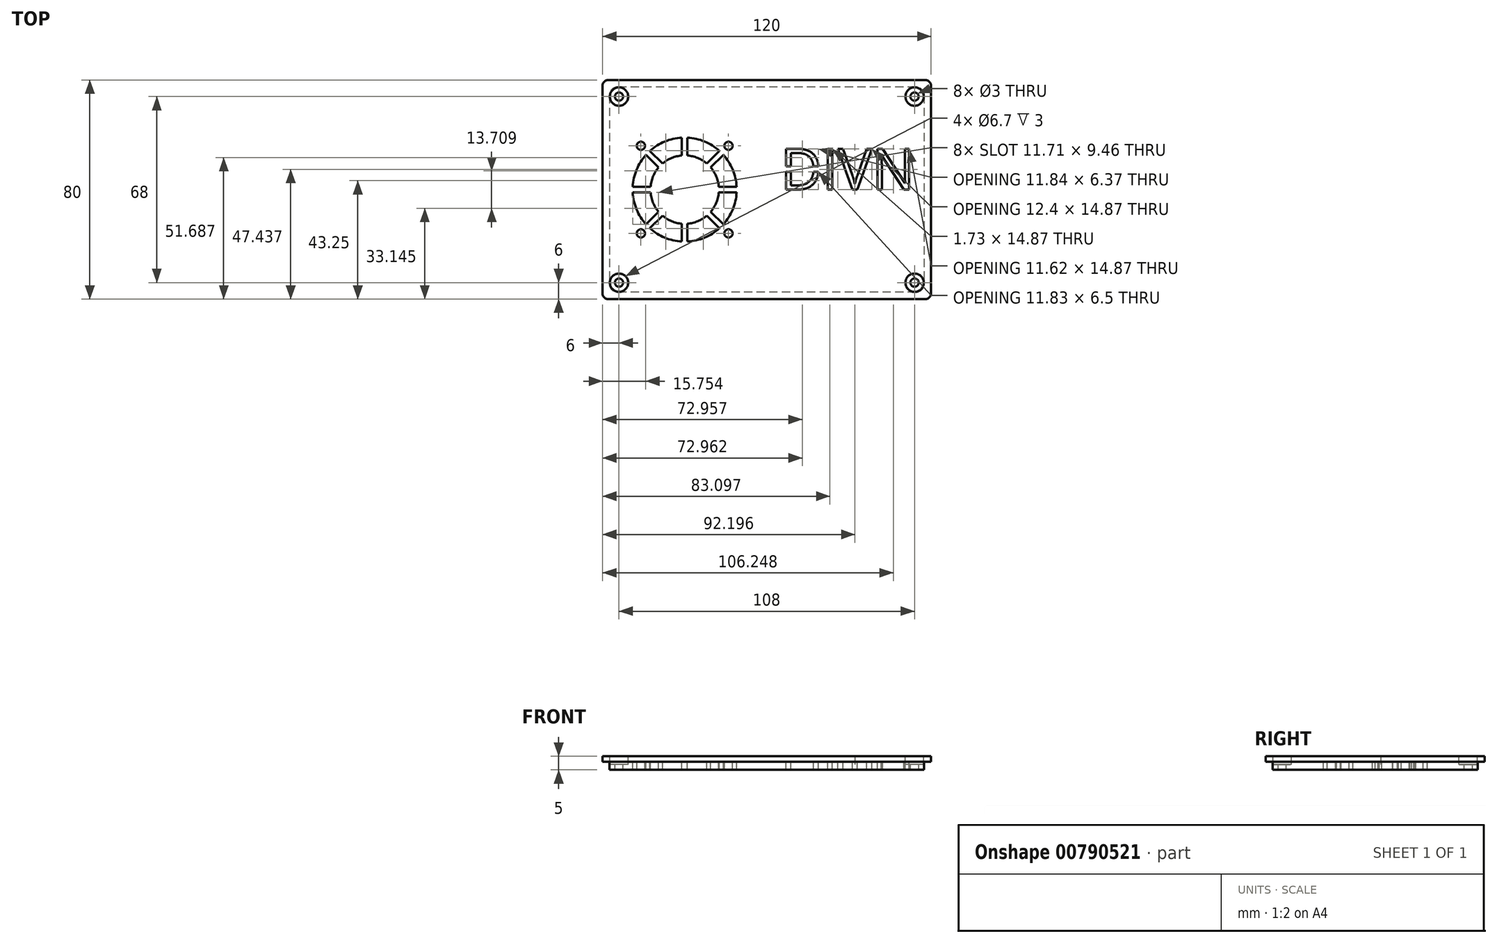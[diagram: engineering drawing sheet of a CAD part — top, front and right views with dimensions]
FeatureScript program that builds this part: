
annotation { "Feature Type Name" : "Feature", "Feature Type Description" : "" }
export const myFeature = defineFeature(function(context is Context, id is Id, definition is map)
    precondition{}
    {
        {
            var Q0;
            Q0=qCreatedBy(makeId("Top.planeOp"),FACE);
            var sketch = newSketch(context, id + "F0", { "sketchPlane" : qUnion([Q0])});
            skLineSegment(sketch, "E0.bottom", {"start": v(60, 40) * mm, "end": v(-60, 40) * mm});
            skLineSegment(sketch, "E0.top", {"start": v(60, -40) * mm, "end": v(-60, -40) * mm});
            skLineSegment(sketch, "E0.left", {"start": v(60, 40) * mm, "end": v(60, -40) * mm});
            skLineSegment(sketch, "E0.right", {"start": v(-60, 40) * mm, "end": v(-60, -40) * mm});
            skPoint(sketch, "E0.middle", {"position": v(0, 0) * mm});
            skLineSegment(sketch, "E1.bottom", {"start": v(57.5, 37.5) * mm, "end": v(-57.5, 37.5) * mm});
            skLineSegment(sketch, "E1.top", {"start": v(57.5, -37.5) * mm, "end": v(-57.5, -37.5) * mm});
            skLineSegment(sketch, "E1.left", {"start": v(57.5, 37.5) * mm, "end": v(57.5, -37.5) * mm});
            skLineSegment(sketch, "E1.right", {"start": v(-57.5, 37.5) * mm, "end": v(-57.5, -37.5) * mm});
            skSolve(sketch);
        }
        {
            var Q0;
            Q0=makeQuery(id+"F0.imprint","IMPRINT",FACE,{"disambiguationData":[TD([[makeQuery(id+"F0.imprint","IMPRINT",EDGE,{"derivedFrom":sQuery(id+"F0.wireOp",EDGE,"E0.bottom")}),1.0]])]});
            extrude(context, id + "F1", {"entities" : qUnion([Q0]), "depth" : 2 * mm, "offsetDistance" : 25 * mm});
        }
        {
            var Q0;
            Q0=makeQuery(id+"F1.opExtrude","CAP_FACE",FACE,{"disambiguationData":[OSD([sQuery(id+"F0.wireOp",EDGE,"E0.bottom"),sQuery(id+"F0.wireOp",EDGE,"E0.top"),sQuery(id+"F0.wireOp",EDGE,"E0.left"),sQuery(id+"F0.wireOp",EDGE,"E0.right"),sQuery(id+"F0.wireOp",EDGE,"E1.bottom"),sQuery(id+"F0.wireOp",EDGE,"E1.top"),sQuery(id+"F0.wireOp",EDGE,"E1.left"),sQuery(id+"F0.wireOp",EDGE,"E1.right")])],"isStart":false});
            var sketch = newSketch(context, id + "F2", { "sketchPlane" : qUnion([Q0])});
            skLineSegment(sketch, "E2.bottom", {"start": v(-57.5, 37.5) * mm, "end": v(57.5, 37.5) * mm});
            skLineSegment(sketch, "E2.top", {"start": v(-57.5, -37.5) * mm, "end": v(57.5, -37.5) * mm});
            skLineSegment(sketch, "E2.left", {"start": v(-57.5, 37.5) * mm, "end": v(-57.5, -37.5) * mm});
            skLineSegment(sketch, "E2.right", {"start": v(57.5, 37.5) * mm, "end": v(57.5, -37.5) * mm});
            skSolve(sketch);
        }
        {
            var Q0;
            Q0=makeQuery(id+"F2.imprint","IMPRINT",FACE,{"disambiguationData":[TD([[makeQuery(id+"F2.imprint","IMPRINT",EDGE,{"derivedFrom":sQuery(id+"F2.wireOp",EDGE,"E2.bottom")}),1.0]])]});
            extrude(context, id + "F3", {"entities" : qUnion([Q0]), "oppositeDirection" : true, "depth" : 5 * mm, "offsetDistance" : 25 * mm});
        }
        {
            var Q0;
            Q0=makeQuery(id+"F3.opExtrude","SWEPT_BODY",BODY,{"disambiguationData":[OSD([sQuery(id+"F2.wireOp",EDGE,"E2.bottom"),sQuery(id+"F2.wireOp",EDGE,"E2.top"),sQuery(id+"F2.wireOp",EDGE,"E2.left"),sQuery(id+"F2.wireOp",EDGE,"E2.right")])]});
            var Q1;
            Q1=makeQuery(id+"F1.opExtrude","SWEPT_BODY",BODY,{"disambiguationData":[OSD([sQuery(id+"F0.wireOp",EDGE,"E0.bottom"),sQuery(id+"F0.wireOp",EDGE,"E0.top"),sQuery(id+"F0.wireOp",EDGE,"E0.left"),sQuery(id+"F0.wireOp",EDGE,"E0.right"),sQuery(id+"F0.wireOp",EDGE,"E1.bottom"),sQuery(id+"F0.wireOp",EDGE,"E1.top"),sQuery(id+"F0.wireOp",EDGE,"E1.left"),sQuery(id+"F0.wireOp",EDGE,"E1.right")])]});
            booleanBodies(context, id + "F4", {"operationType" : BooleanOperationType.UNION, "tools" : qUnion([Q0, Q1])});
        }
        {
            var Q0;
            Q0=makeQuery(id+"F3.opExtrude","SWEPT_EDGE",EDGE,{"disambiguationData":[OSD([sQuery(id+"F2.wireOp",EDGE,"E2.bottom"),sQuery(id+"F2.wireOp",EDGE,"E2.left")])]});
            var Q1;
            Q1=makeQuery(id+"F3.opExtrude","SWEPT_EDGE",EDGE,{"disambiguationData":[OSD([sQuery(id+"F2.wireOp",EDGE,"E2.top"),sQuery(id+"F2.wireOp",EDGE,"E2.left")])]});
            var Q2;
            Q2=makeQuery(id+"F3.opExtrude","SWEPT_EDGE",EDGE,{"disambiguationData":[OSD([sQuery(id+"F2.wireOp",EDGE,"E2.top"),sQuery(id+"F2.wireOp",EDGE,"E2.right")])]});
            var Q3;
            Q3=makeQuery(id+"F3.opExtrude","SWEPT_EDGE",EDGE,{"disambiguationData":[OSD([sQuery(id+"F2.wireOp",EDGE,"E2.bottom"),sQuery(id+"F2.wireOp",EDGE,"E2.right")])]});
            fillet(context, id + "F5", {"entities" : qUnion([Q0, Q1, Q2, Q3]), "radius" : 3 * mm, "tangentPropagation" : true, "allowEdgeOverflow" : false});
        }
        {
            var Q0;
            Q0=makeQuery(id+"F1.opExtrude","SWEPT_EDGE",EDGE,{"disambiguationData":[OSD([sQuery(id+"F0.wireOp",EDGE,"E0.bottom"),sQuery(id+"F0.wireOp",EDGE,"E0.left")])]});
            var Q1;
            Q1=makeQuery(id+"F1.opExtrude","SWEPT_EDGE",EDGE,{"disambiguationData":[OSD([sQuery(id+"F0.wireOp",EDGE,"E0.top"),sQuery(id+"F0.wireOp",EDGE,"E0.left")])]});
            var Q2;
            Q2=makeQuery(id+"F1.opExtrude","SWEPT_EDGE",EDGE,{"disambiguationData":[OSD([sQuery(id+"F0.wireOp",EDGE,"E0.top"),sQuery(id+"F0.wireOp",EDGE,"E0.right")])]});
            var Q3;
            Q3=makeQuery(id+"F1.opExtrude","SWEPT_EDGE",EDGE,{"disambiguationData":[OSD([sQuery(id+"F0.wireOp",EDGE,"E0.bottom"),sQuery(id+"F0.wireOp",EDGE,"E0.right")])]});
            fillet(context, id + "F6", {"entities" : qUnion([Q0, Q1, Q2, Q3]), "radius" : 2 * mm, "tangentPropagation" : true, "allowEdgeOverflow" : false});
        }
        {
            var Q0;
            Q0=makeQuery(id+"F4.opBoolean","MERGE",FACE,{"derivedFrom":[makeQuery(id+"F1.opExtrude","CAP_FACE",FACE,{"disambiguationData":[OSD([sQuery(id+"F0.wireOp",EDGE,"E0.bottom"),sQuery(id+"F0.wireOp",EDGE,"E0.top"),sQuery(id+"F0.wireOp",EDGE,"E0.left"),sQuery(id+"F0.wireOp",EDGE,"E0.right"),sQuery(id+"F0.wireOp",EDGE,"E1.bottom"),sQuery(id+"F0.wireOp",EDGE,"E1.top"),sQuery(id+"F0.wireOp",EDGE,"E1.left"),sQuery(id+"F0.wireOp",EDGE,"E1.right")])],"isStart":false}),makeQuery(id+"F3.opExtrude","CAP_FACE",FACE,{"disambiguationData":[OSD([sQuery(id+"F2.wireOp",EDGE,"E2.bottom"),sQuery(id+"F2.wireOp",EDGE,"E2.top"),sQuery(id+"F2.wireOp",EDGE,"E2.left"),sQuery(id+"F2.wireOp",EDGE,"E2.right")])],"isStart":true})]});
            var sketch = newSketch(context, id + "F7", { "sketchPlane" : qUnion([Q0])});
            skCircle(sketch, "E3", {"center": v(-54, 34) * mm, "radius": 1.5 * mm});
            skCircle(sketch, "E4", {"center": v(54, 34) * mm, "radius": 1.5 * mm});
            skCircle(sketch, "E5", {"center": v(54, -34) * mm, "radius": 1.5 * mm});
            skCircle(sketch, "E6", {"center": v(-54, -34) * mm, "radius": 1.5 * mm});
            skPoint(sketch, "E7.middle", {"position": v(-30, 0) * mm});
            skPoint(sketch, "E8.middle", {"position": v(25.11, 0) * mm});
            skSolve(sketch);
        }
        {
            var Q0;
            Q0=makeQuery(id+"F7.imprint","IMPRINT",FACE,{"disambiguationData":[TD([[makeQuery(id+"F7.imprint","IMPRINT",EDGE,{"derivedFrom":sQuery(id+"F7.wireOp",EDGE,"E3")}),1.0]])]});
            var Q1;
            Q1=makeQuery(id+"F7.imprint","IMPRINT",FACE,{"disambiguationData":[TD([[makeQuery(id+"F7.imprint","IMPRINT",EDGE,{"derivedFrom":sQuery(id+"F7.wireOp",EDGE,"E4")}),1.0]])]});
            var Q2;
            Q2=makeQuery(id+"F7.imprint","IMPRINT",FACE,{"disambiguationData":[TD([[makeQuery(id+"F7.imprint","IMPRINT",EDGE,{"derivedFrom":sQuery(id+"F7.wireOp",EDGE,"E6")}),1.0]])]});
            var Q3;
            Q3=makeQuery(id+"F7.imprint","IMPRINT",FACE,{"disambiguationData":[TD([[makeQuery(id+"F7.imprint","IMPRINT",EDGE,{"derivedFrom":sQuery(id+"F7.wireOp",EDGE,"E5")}),1.0]])]});
            var Q4;
            Q4=sQuery(id+"F7.wireOp",EDGE,"E3");
            var Q5;
            Q5=sQuery(id+"F7.wireOp",EDGE,"E4");
            var Q6;
            Q6=sQuery(id+"F7.wireOp",EDGE,"E5");
            var Q7;
            Q7=sQuery(id+"F7.wireOp",EDGE,"E6");
            extrude(context, id + "F8", {"entities" : qUnion([Q0, Q1, Q2, Q3]), "operationType" : NewBodyOperationType.REMOVE, "surfaceEntities" : qUnion([Q4, Q5, Q6, Q7]), "oppositeDirection" : true, "depth" : 25 * mm, "offsetDistance" : 25 * mm});
        }
        {
            var Q0;
            Q0=makeQuery(id+"F4.opBoolean","MERGE",FACE,{"derivedFrom":[makeQuery(id+"F1.opExtrude","CAP_FACE",FACE,{"disambiguationData":[OSD([sQuery(id+"F0.wireOp",EDGE,"E0.bottom"),sQuery(id+"F0.wireOp",EDGE,"E0.top"),sQuery(id+"F0.wireOp",EDGE,"E0.left"),sQuery(id+"F0.wireOp",EDGE,"E0.right"),sQuery(id+"F0.wireOp",EDGE,"E1.bottom"),sQuery(id+"F0.wireOp",EDGE,"E1.top"),sQuery(id+"F0.wireOp",EDGE,"E1.left"),sQuery(id+"F0.wireOp",EDGE,"E1.right")])],"isStart":false}),makeQuery(id+"F3.opExtrude","CAP_FACE",FACE,{"disambiguationData":[OSD([sQuery(id+"F2.wireOp",EDGE,"E2.bottom"),sQuery(id+"F2.wireOp",EDGE,"E2.top"),sQuery(id+"F2.wireOp",EDGE,"E2.left"),sQuery(id+"F2.wireOp",EDGE,"E2.right")])],"isStart":true})]});
            var sketch = newSketch(context, id + "F9", { "sketchPlane" : qUnion([Q0])});
            skCircle(sketch, "E9", {"center": v(-54, 34) * mm, "radius": 3.35 * mm});
            skCircle(sketch, "E10", {"center": v(54, 34) * mm, "radius": 3.35 * mm});
            skCircle(sketch, "E11", {"center": v(54, -34) * mm, "radius": 3.35 * mm});
            skCircle(sketch, "E12", {"center": v(-54, -34) * mm, "radius": 3.35 * mm});
            skSolve(sketch);
        }
        {
            var Q0;
            Q0=makeQuery(id+"F9.imprint","IMPRINT",FACE,{"disambiguationData":[TD([[makeQuery(id+"F9.imprint","IMPRINT",EDGE,{"derivedFrom":sQuery(id+"F9.wireOp",EDGE,"E9")}),1.0]])]});
            var Q1;
            Q1=makeQuery(id+"F9.imprint","IMPRINT",FACE,{"disambiguationData":[TD([[makeQuery(id+"F9.imprint","IMPRINT",EDGE,{"derivedFrom":sQuery(id+"F9.wireOp",EDGE,"E10")}),1.0]])]});
            var Q2;
            Q2=makeQuery(id+"F9.imprint","IMPRINT",FACE,{"disambiguationData":[TD([[makeQuery(id+"F9.imprint","IMPRINT",EDGE,{"derivedFrom":sQuery(id+"F9.wireOp",EDGE,"E11")}),1.0]])]});
            var Q3;
            Q3=makeQuery(id+"F9.imprint","IMPRINT",FACE,{"disambiguationData":[TD([[makeQuery(id+"F9.imprint","IMPRINT",EDGE,{"derivedFrom":sQuery(id+"F9.wireOp",EDGE,"E12")}),1.0]])]});
            extrude(context, id + "F10", {"entities" : qUnion([Q0, Q1, Q2, Q3]), "operationType" : NewBodyOperationType.REMOVE, "oppositeDirection" : true, "depth" : 3 * mm, "offsetDistance" : 25 * mm});
        }
        {
            var Q0;
            Q0=makeQuery(id+"F4.opBoolean","MERGE",FACE,{"derivedFrom":[makeQuery(id+"F1.opExtrude","CAP_FACE",FACE,{"disambiguationData":[OSD([sQuery(id+"F0.wireOp",EDGE,"E0.bottom"),sQuery(id+"F0.wireOp",EDGE,"E0.top"),sQuery(id+"F0.wireOp",EDGE,"E0.left"),sQuery(id+"F0.wireOp",EDGE,"E0.right"),sQuery(id+"F0.wireOp",EDGE,"E1.bottom"),sQuery(id+"F0.wireOp",EDGE,"E1.top"),sQuery(id+"F0.wireOp",EDGE,"E1.left"),sQuery(id+"F0.wireOp",EDGE,"E1.right")])],"isStart":false}),makeQuery(id+"F3.opExtrude","CAP_FACE",FACE,{"disambiguationData":[OSD([sQuery(id+"F2.wireOp",EDGE,"E2.bottom"),sQuery(id+"F2.wireOp",EDGE,"E2.top"),sQuery(id+"F2.wireOp",EDGE,"E2.left"),sQuery(id+"F2.wireOp",EDGE,"E2.right")])],"isStart":true})]});
            var sketch = newSketch(context, id + "F11", { "sketchPlane" : qUnion([Q0])});
            skLineSegment(sketch, "E13.bottom", {"start": v(-50, 20) * mm, "end": v(-10, 20) * mm, "construction": true});
            skLineSegment(sketch, "E13.top", {"start": v(-50, -20) * mm, "end": v(-10, -20) * mm, "construction": true});
            skLineSegment(sketch, "E13.left", {"start": v(-50, 20) * mm, "end": v(-50, -20) * mm, "construction": true});
            skLineSegment(sketch, "E13.right", {"start": v(-10, 20) * mm, "end": v(-10, -20) * mm, "construction": true});
            skCircle(sketch, "E14", {"center": v(-46, 16) * mm, "radius": 1.5 * mm});
            skCircle(sketch, "E15", {"center": v(-14, 16) * mm, "radius": 1.5 * mm});
            skCircle(sketch, "E16", {"center": v(-14, -16) * mm, "radius": 1.5 * mm});
            skCircle(sketch, "E17", {"center": v(-46, -16) * mm, "radius": 1.5 * mm});
            skCircle(sketch, "E18", {"center": v(-30, 0) * mm, "radius": 19 * mm});
            skPoint(sketch, "E18.centerSnap0", {"position": v(-30, 20) * mm});
            skPoint(sketch, "E18.centerSnap1", {"position": v(-10, 0) * mm});
            skCircle(sketch, "E19", {"center": v(-30, 0) * mm, "radius": 12.5 * mm});
            skLineSegment(sketch, "E20.bottom", {"start": v(-29, 19.5) * mm, "end": v(-31, 19.5) * mm});
            skLineSegment(sketch, "E20.top", {"start": v(-29, 12) * mm, "end": v(-31, 12) * mm});
            skLineSegment(sketch, "E20.left", {"start": v(-29, 19.5) * mm, "end": v(-29, 12) * mm});
            skLineSegment(sketch, "E20.right", {"start": v(-31, 19.5) * mm, "end": v(-31, 12) * mm});
            skPoint(sketch, "E20.middle", {"position": v(-30, 15.75) * mm});
            skPoint(sketch, "E21.1.0", {"position": v(-41.14, 11.14) * mm});
            skLineSegment(sketch, "E21.1.1", {"start": v(-43.08, 14.5) * mm, "end": v(-44.5, 13.08) * mm});
            skLineSegment(sketch, "E21.1.2", {"start": v(-44.5, 13.08) * mm, "end": v(-39.2, 7.78) * mm});
            skLineSegment(sketch, "E21.1.3", {"start": v(-43.08, 14.5) * mm, "end": v(-37.78, 9.2) * mm});
            skLineSegment(sketch, "E21.1.4", {"start": v(-37.78, 9.2) * mm, "end": v(-39.2, 7.78) * mm});
            skPoint(sketch, "E21.2.0", {"position": v(-45.75, 0) * mm});
            skLineSegment(sketch, "E21.2.1", {"start": v(-49.5, 1) * mm, "end": v(-49.5, -1) * mm});
            skLineSegment(sketch, "E21.2.2", {"start": v(-49.5, -1) * mm, "end": v(-42, -1) * mm});
            skLineSegment(sketch, "E21.2.3", {"start": v(-49.5, 1) * mm, "end": v(-42, 1) * mm});
            skLineSegment(sketch, "E21.2.4", {"start": v(-42, 1) * mm, "end": v(-42, -1) * mm});
            skPoint(sketch, "E21.3.0", {"position": v(-41.14, -11.14) * mm});
            skLineSegment(sketch, "E21.3.1", {"start": v(-44.5, -13.08) * mm, "end": v(-43.08, -14.5) * mm});
            skLineSegment(sketch, "E21.3.2", {"start": v(-43.08, -14.5) * mm, "end": v(-37.78, -9.2) * mm});
            skLineSegment(sketch, "E21.3.3", {"start": v(-44.5, -13.08) * mm, "end": v(-39.2, -7.78) * mm});
            skLineSegment(sketch, "E21.3.4", {"start": v(-39.2, -7.78) * mm, "end": v(-37.78, -9.2) * mm});
            skPoint(sketch, "E21.4.0", {"position": v(-30, -15.75) * mm});
            skLineSegment(sketch, "E21.4.1", {"start": v(-31, -19.5) * mm, "end": v(-29, -19.5) * mm});
            skLineSegment(sketch, "E21.4.2", {"start": v(-29, -19.5) * mm, "end": v(-29, -12) * mm});
            skLineSegment(sketch, "E21.4.3", {"start": v(-31, -19.5) * mm, "end": v(-31, -12) * mm});
            skLineSegment(sketch, "E21.4.4", {"start": v(-31, -12) * mm, "end": v(-29, -12) * mm});
            skPoint(sketch, "E21.5.0", {"position": v(-18.86, -11.14) * mm});
            skLineSegment(sketch, "E21.5.1", {"start": v(-16.92, -14.5) * mm, "end": v(-15.5, -13.08) * mm});
            skLineSegment(sketch, "E21.5.2", {"start": v(-15.5, -13.08) * mm, "end": v(-20.8, -7.78) * mm});
            skLineSegment(sketch, "E21.5.3", {"start": v(-16.92, -14.5) * mm, "end": v(-22.22, -9.2) * mm});
            skLineSegment(sketch, "E21.5.4", {"start": v(-22.22, -9.2) * mm, "end": v(-20.8, -7.78) * mm});
            skPoint(sketch, "E21.6.0", {"position": v(-14.25, 0) * mm});
            skLineSegment(sketch, "E21.6.1", {"start": v(-10.5, -1) * mm, "end": v(-10.5, 1) * mm});
            skLineSegment(sketch, "E21.6.2", {"start": v(-10.5, 1) * mm, "end": v(-18, 1) * mm});
            skLineSegment(sketch, "E21.6.3", {"start": v(-10.5, -1) * mm, "end": v(-18, -1) * mm});
            skLineSegment(sketch, "E21.6.4", {"start": v(-18, -1) * mm, "end": v(-18, 1) * mm});
            skPoint(sketch, "E21.7.0", {"position": v(-18.86, 11.14) * mm});
            skLineSegment(sketch, "E21.7.1", {"start": v(-15.5, 13.08) * mm, "end": v(-16.92, 14.5) * mm});
            skLineSegment(sketch, "E21.7.2", {"start": v(-16.92, 14.5) * mm, "end": v(-22.22, 9.2) * mm});
            skLineSegment(sketch, "E21.7.3", {"start": v(-15.5, 13.08) * mm, "end": v(-20.8, 7.78) * mm});
            skLineSegment(sketch, "E21.7.4", {"start": v(-20.8, 7.78) * mm, "end": v(-22.22, 9.2) * mm});
            skText(sketch, "E22", { "text": "DIVN\n", "fontName": "OpenSans-Regular.ttf"});
            skLineSegment(sketch, "E23.bottom", {"start": v(1.83, 8.5) * mm, "end": v(19.83, 8.5) * mm});
            skLineSegment(sketch, "E23.top", {"start": v(1.83, 6.5) * mm, "end": v(19.83, 6.5) * mm});
            skLineSegment(sketch, "E23.left", {"start": v(1.83, 8.5) * mm, "end": v(1.83, 6.5) * mm});
            skLineSegment(sketch, "E23.right", {"start": v(19.83, 8.5) * mm, "end": v(19.83, 6.5) * mm});
            skPoint(sketch, "E23.middle", {"position": v(10.83, 7.5) * mm});
            skPoint(sketch, "E23.middle.positionSnap0", {"position": v(5, 7.5) * mm});
            skPoint(sketch, "E23.centerSnap0", {"position": v(5, 7.5) * mm});
            const initialGuessF11  = {"E22": [0.005, 0, 1, 0, 0.015]};
            skSetInitialGuess(sketch, initialGuessF11);
            skSolve(sketch);
        }
        {
            var Q0;
            {var subQ0=sQuery(id+"F11.wireOp",EDGE,"E21.7.3");var subQ1=sQuery(id+"F11.wireOp",EDGE,"E18");var subQ2=makeQuery(id+"F11.imprint","INTERSECT",VERTEX,{"derivedFrom":[subQ1,subQ0]});Q0=makeQuery(id+"F11.imprint","IMPRINT",FACE,{"disambiguationData":[TD([[makeQuery(id+"F11.imprint","IMPRINT",EDGE,{"disambiguationData":[TD([[subQ2,1.0]])],"derivedFrom":subQ1}),1.0]])]});}
            var Q1;
            Q1=makeQuery(id+"F11.imprint","IMPRINT",FACE,{"disambiguationData":[TD([[makeQuery(id+"F11.imprint","IMPRINT",EDGE,{"derivedFrom":sQuery(id+"F11.wireOp",EDGE,"E15")}),1.0]])]});
            var Q2;
            {var subQ0=sQuery(id+"F11.wireOp",EDGE,"E21.7.2");var subQ1=sQuery(id+"F11.wireOp",EDGE,"E18");var subQ2=makeQuery(id+"F11.imprint","INTERSECT",VERTEX,{"derivedFrom":[subQ1,subQ0]});Q2=makeQuery(id+"F11.imprint","IMPRINT",FACE,{"disambiguationData":[TD([[makeQuery(id+"F11.imprint","IMPRINT",EDGE,{"disambiguationData":[TD([[subQ2,-1.0]])],"derivedFrom":subQ1}),1.0]])]});}
            var Q3;
            {var subQ0=sQuery(id+"F11.wireOp",EDGE,"E20.right");var subQ1=sQuery(id+"F11.wireOp",EDGE,"E18");var subQ2=makeQuery(id+"F11.imprint","INTERSECT",VERTEX,{"derivedFrom":[subQ1,subQ0]});Q3=makeQuery(id+"F11.imprint","IMPRINT",FACE,{"disambiguationData":[TD([[makeQuery(id+"F11.imprint","IMPRINT",EDGE,{"disambiguationData":[TD([[subQ2,-1.0]])],"derivedFrom":subQ1}),1.0]])]});}
            var Q4;
            {var subQ0=sQuery(id+"F11.wireOp",EDGE,"E21.1.2");var subQ1=sQuery(id+"F11.wireOp",EDGE,"E18");var subQ2=makeQuery(id+"F11.imprint","INTERSECT",VERTEX,{"derivedFrom":[subQ1,subQ0]});Q4=makeQuery(id+"F11.imprint","IMPRINT",FACE,{"disambiguationData":[TD([[makeQuery(id+"F11.imprint","IMPRINT",EDGE,{"disambiguationData":[TD([[subQ2,-1.0]])],"derivedFrom":subQ1}),1.0]])]});}
            var Q5;
            {var subQ0=sQuery(id+"F11.wireOp",EDGE,"E21.2.2");var subQ1=sQuery(id+"F11.wireOp",EDGE,"E18");var subQ2=makeQuery(id+"F11.imprint","INTERSECT",VERTEX,{"derivedFrom":[subQ1,subQ0]});Q5=makeQuery(id+"F11.imprint","IMPRINT",FACE,{"disambiguationData":[TD([[makeQuery(id+"F11.imprint","IMPRINT",EDGE,{"disambiguationData":[TD([[subQ2,-1.0]])],"derivedFrom":subQ1}),1.0]])]});}
            var Q6;
            {var subQ0=sQuery(id+"F11.wireOp",EDGE,"E21.3.2");var subQ1=sQuery(id+"F11.wireOp",EDGE,"E18");var subQ2=makeQuery(id+"F11.imprint","INTERSECT",VERTEX,{"derivedFrom":[subQ1,subQ0]});Q6=makeQuery(id+"F11.imprint","IMPRINT",FACE,{"disambiguationData":[TD([[makeQuery(id+"F11.imprint","IMPRINT",EDGE,{"disambiguationData":[TD([[subQ2,-1.0]])],"derivedFrom":subQ1}),1.0]])]});}
            var Q7;
            {var subQ0=sQuery(id+"F11.wireOp",EDGE,"E21.4.2");var subQ1=sQuery(id+"F11.wireOp",EDGE,"E18");var subQ2=makeQuery(id+"F11.imprint","INTERSECT",VERTEX,{"derivedFrom":[subQ1,subQ0]});Q7=makeQuery(id+"F11.imprint","IMPRINT",FACE,{"disambiguationData":[TD([[makeQuery(id+"F11.imprint","IMPRINT",EDGE,{"disambiguationData":[TD([[subQ2,-1.0]])],"derivedFrom":subQ1}),1.0]])]});}
            var Q8;
            {var subQ0=sQuery(id+"F11.wireOp",EDGE,"E21.5.2");var subQ1=sQuery(id+"F11.wireOp",EDGE,"E18");var subQ2=makeQuery(id+"F11.imprint","INTERSECT",VERTEX,{"derivedFrom":[subQ1,subQ0]});Q8=makeQuery(id+"F11.imprint","IMPRINT",FACE,{"disambiguationData":[TD([[makeQuery(id+"F11.imprint","IMPRINT",EDGE,{"disambiguationData":[TD([[subQ2,-1.0]])],"derivedFrom":subQ1}),1.0]])]});}
            var Q9;
            Q9=makeQuery(id+"F11.imprint","IMPRINT",FACE,{"disambiguationData":[TD([[makeQuery(id+"F11.imprint","IMPRINT",EDGE,{"derivedFrom":sQuery(id+"F11.wireOp",EDGE,"E16")}),1.0]])]});
            var Q10;
            Q10=makeQuery(id+"F11.imprint","IMPRINT",FACE,{"disambiguationData":[TD([[makeQuery(id+"F11.imprint","IMPRINT",EDGE,{"derivedFrom":sQuery(id+"F11.wireOp",EDGE,"E17")}),1.0]])]});
            var Q11;
            Q11=makeQuery(id+"F11.imprint","IMPRINT",FACE,{"disambiguationData":[TD([[makeQuery(id+"F11.imprint","IMPRINT",EDGE,{"derivedFrom":sQuery(id+"F11.wireOp",EDGE,"E14")}),1.0]])]});
            var Q12;
            Q12=makeQuery(id+"F11.imprint","IMPRINT",FACE,{"disambiguationData":[TD([[makeQuery(id+"F11.imprint","IMPRINT",EDGE,{"derivedFrom":sQuery(id+"F11.wireOp",EDGE,"E22.sketch_text.stroke-14")}),-1.0]])]});
            var Q13;
            Q13=makeQuery(id+"F11.imprint","IMPRINT",FACE,{"disambiguationData":[TD([[makeQuery(id+"F11.imprint","IMPRINT",EDGE,{"derivedFrom":sQuery(id+"F11.wireOp",EDGE,"E22.sketch_text.stroke-18")}),-1.0]])]});
            var Q14;
            Q14=makeQuery(id+"F11.imprint","IMPRINT",FACE,{"disambiguationData":[TD([[makeQuery(id+"F11.imprint","IMPRINT",EDGE,{"derivedFrom":sQuery(id+"F11.wireOp",EDGE,"E22.sketch_text.stroke-27")}),-1.0]])]});
            var Q15;
            {var subQ6=sQuery(id+"F11.wireOp",EDGE,"E22.sketch_text.stroke-4");Q15=makeQuery(id+"F11.imprint","IMPRINT",FACE,{"disambiguationData":[TD([[makeQuery(id+"F11.imprint","IMPRINT",EDGE,{"derivedFrom":subQ6}),-1.0]])]});}
            var Q16;
            {var subQ8=sQuery(id+"F11.wireOp",EDGE,"E22.sketch_text.stroke-1");Q16=makeQuery(id+"F11.imprint","IMPRINT",FACE,{"disambiguationData":[TD([[makeQuery(id+"F11.imprint","IMPRINT",EDGE,{"derivedFrom":subQ8}),-1.0]])]});}
            extrude(context, id + "F12", {"entities" : qUnion([Q0, Q1, Q2, Q3, Q4, Q5, Q6, Q7, Q8, Q9, Q10, Q11, Q12, Q13, Q14, Q15, Q16]), "operationType" : NewBodyOperationType.REMOVE, "oppositeDirection" : true, "depth" : 25 * mm, "offsetDistance" : 25 * mm});
        }
    });
